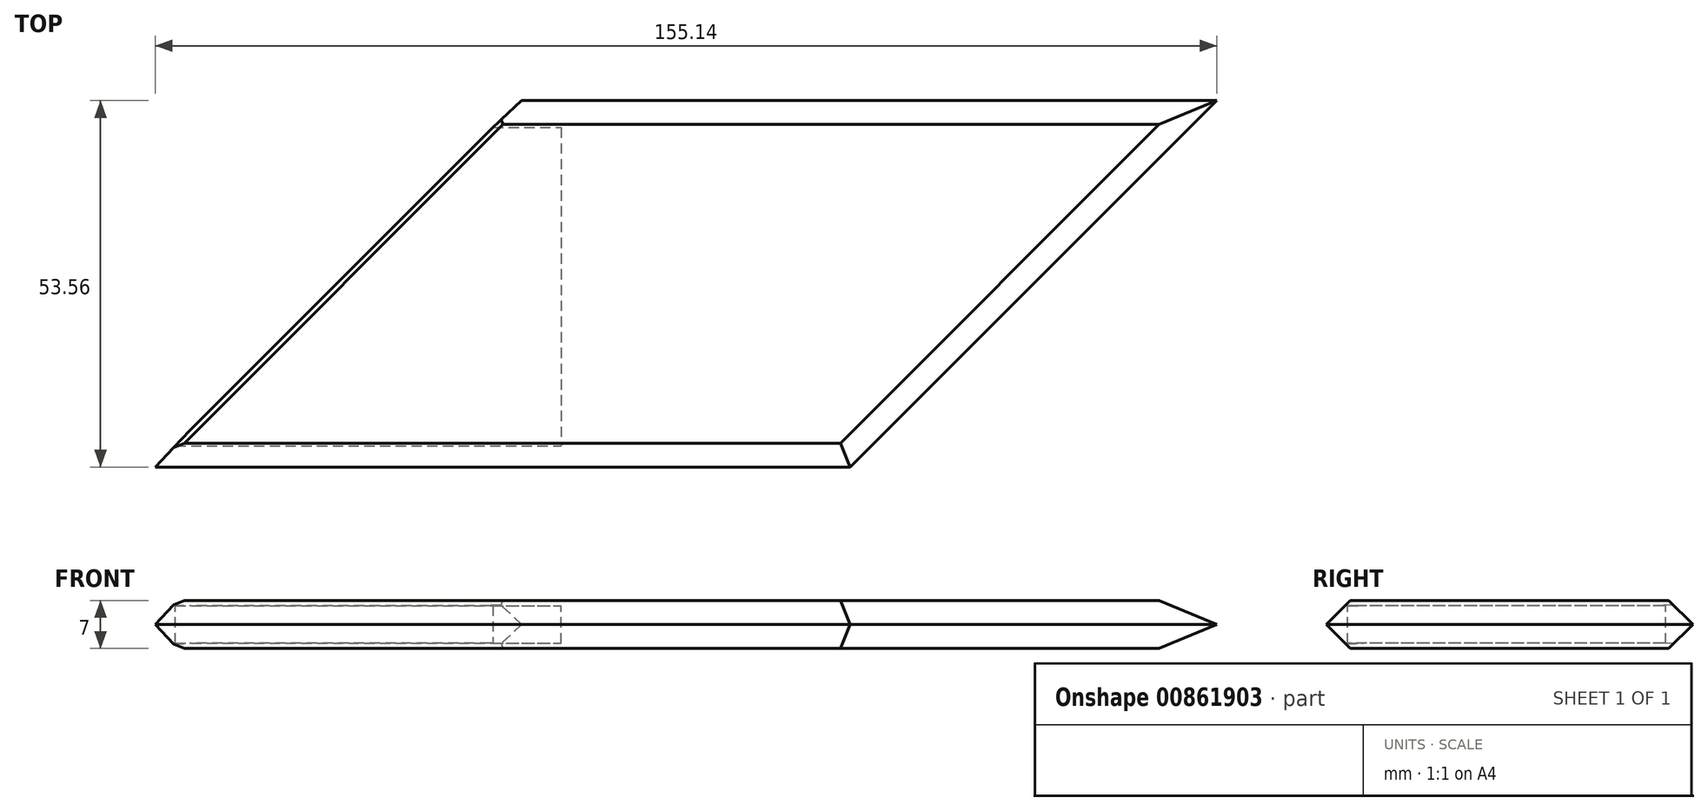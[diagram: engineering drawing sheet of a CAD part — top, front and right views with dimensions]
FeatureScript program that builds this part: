
annotation { "Feature Type Name" : "Feature", "Feature Type Description" : "" }
export const myFeature = defineFeature(function(context is Context, id is Id, definition is map)
    precondition{}
    {
        {
            var Q0;
            Q0=qCreatedBy(makeId("Top.planeOp"),FACE);
            cPlane(context, id + "F0", {"entities" : qUnion([Q0]), "cplaneType" : CPlaneType.OFFSET, "offset" : 3.5 * mm, "width" : 150 * mm, "height" : 150 * mm});
        }
        {
            var Q0;
            Q0=qCreatedBy(id+"F0.planeOp",FACE);
            var sketch = newSketch(context, id + "F1", { "sketchPlane" : qUnion([Q0])});
            skLineSegment(sketch, "E0", {"start": v(32.38, -28.28) * mm, "end": v(88.95, 28.28) * mm});
            skLineSegment(sketch, "E1", {"start": v(32.38, -28.28) * mm, "end": v(-77.62, -28.28) * mm});
            skLineSegment(sketch, "E2", {"start": v(88.95, 28.28) * mm, "end": v(-21.05, 28.28) * mm});
            skLineSegment(sketch, "E3", {"start": v(-21.05, 28.28) * mm, "end": v(-77.62, -28.28) * mm});
            skLineSegment(sketch, "E4", {"start": v(32.38, -28.28) * mm, "end": v(60.67, 0) * mm});
            skLineSegment(sketch, "E5", {"start": v(-9.09, -28.28) * mm, "end": v(-9.09, 28.28) * mm, "construction": true});
            skLineSegment(sketch, "E6", {"start": v(11.8, -28.28) * mm, "end": v(11.8, 0) * mm});
            skSolve(sketch);
        }
        {
            var Q0;
            Q0=makeQuery(id+"F1.imprint","IMPRINT",FACE,{"disambiguationData":[TD([[makeQuery(id+"F1.imprint","IMPRINT",EDGE,{"derivedFrom":sQuery(id+"F1.wireOp",EDGE,"E0")}),1.0]])]});
            extrude(context, id + "F2", {"entities" : qUnion([Q0]), "depth" : 3.5 * mm, "offsetDistance" : 25 * mm});
        }
        {
            var Q0;
            Q0=makeQuery(id+"F2.opExtrude","CAP_FACE",FACE,{"disambiguationData":[OSD([sQuery(id+"F1.wireOp",EDGE,"E0"),sQuery(id+"F1.wireOp",EDGE,"E1"),sQuery(id+"F1.wireOp",EDGE,"E2"),sQuery(id+"F1.wireOp",EDGE,"E3")])],"isStart":true});
            chamfer(context, id + "F3", {"entities" : qUnion([Q0]), "width" : 5 * mm, "tangentPropagation" : true});
        }
        {
            var Q0;
            Q0=makeQuery(id+"F2.opExtrude","CAP_FACE",FACE,{"disambiguationData":[OSD([sQuery(id+"F1.wireOp",EDGE,"E0"),sQuery(id+"F1.wireOp",EDGE,"E1"),sQuery(id+"F1.wireOp",EDGE,"E2"),sQuery(id+"F1.wireOp",EDGE,"E3")])],"isStart":true});
            var sketch = newSketch(context, id + "F4", { "sketchPlane" : qUnion([Q0])});
            skLineSegment(sketch, "E7", {"start": v(-60.92, 17.37) * mm, "end": v(-71.56, 28.64) * mm});
            skLineSegment(sketch, "E8", {"start": v(-71.56, 28.64) * mm, "end": v(-75.4, 28.64) * mm});
            skLineSegment(sketch, "E9", {"start": v(-75.4, 28.64) * mm, "end": v(-72.63, 14.89) * mm});
            skLineSegment(sketch, "E10", {"start": v(-72.63, 14.89) * mm, "end": v(-60.92, 17.37) * mm});
            skLineSegment(sketch, "E11.MirrorCS", {"start": v(-71.56, -28.64) * mm, "end": v(-75.4, -28.64) * mm});
            skLineSegment(sketch, "E12.MirrorCS", {"start": v(-75.4, -28.64) * mm, "end": v(-72.63, -14.89) * mm});
            skLineSegment(sketch, "E13.MirrorCS", {"start": v(-72.63, -14.89) * mm, "end": v(-60.92, -17.37) * mm});
            skLineSegment(sketch, "E14.MirrorCS", {"start": v(-60.92, -17.37) * mm, "end": v(-71.56, -28.64) * mm});
            skLineSegment(sketch, "E15", {"start": v(-42.26, 0) * mm, "end": v(-56.59, -14.32) * mm});
            skLineSegment(sketch, "E16", {"start": v(-42.26, 0) * mm, "end": v(-58.96, 0) * mm});
            skLineSegment(sketch, "E17.MirrorCS", {"start": v(-27.38, -30.37) * mm, "end": v(-24.9, -18.65) * mm});
            skLineSegment(sketch, "E18.MirrorCS", {"start": v(-13.62, -33.13) * mm, "end": v(-27.38, -30.37) * mm});
            skLineSegment(sketch, "E19.MirrorCS", {"start": v(-24.9, -18.65) * mm, "end": v(-13.62, -29.3) * mm});
            skLineSegment(sketch, "E20.MirrorCS", {"start": v(-13.62, -29.3) * mm, "end": v(-13.62, -33.13) * mm});
            skSolve(sketch);
        }
        {
            var Q0;
            Q0=makeQuery(id+"F2.opExtrude","CAP_FACE",FACE,{"disambiguationData":[OSD([sQuery(id+"F1.wireOp",EDGE,"E0"),sQuery(id+"F1.wireOp",EDGE,"E1"),sQuery(id+"F1.wireOp",EDGE,"E2"),sQuery(id+"F1.wireOp",EDGE,"E3"),sQuery(id+"F1.wireOp",EDGE,"E4")])],"isStart":false});
            var sketch = newSketch(context, id + "F5", { "sketchPlane" : qUnion([Q0])});
            skLineSegment(sketch, "E21.bottom", {"start": v(-67.31, 22.83) * mm, "end": v(27.88, 22.83) * mm});
            skLineSegment(sketch, "E21.top", {"start": v(-67.31, -23.67) * mm, "end": v(27.88, -23.67) * mm});
            skLineSegment(sketch, "E21.left", {"start": v(-67.31, 22.83) * mm, "end": v(-67.31, -23.67) * mm});
            skLineSegment(sketch, "E21.right", {"start": v(27.88, 22.83) * mm, "end": v(27.88, -23.67) * mm});
            skSolve(sketch);
        }
        {
            var Q0;
            Q0 = qSketchRegion(id + "F5", true);
            extrude(context, id + "F6", {"entities" : qUnion([Q0]), "operationType" : NewBodyOperationType.REMOVE, "oppositeDirection" : true, "depth" : 2.75 * mm, "offsetDistance" : 25 * mm});
        }
        {
            var Q0;
            Q0=makeQuery(id+"F4.imprint","IMPRINT",FACE,{"disambiguationData":[TD([[makeQuery(id+"F4.imprint","IMPRINT",EDGE,{"derivedFrom":sQuery(id+"F4.wireOp",EDGE,"E17.MirrorCS")}),-1.0]])]});
            var Q1;
            Q1=makeQuery(id+"F4.imprint","IMPRINT",FACE,{"disambiguationData":[TD([[makeQuery(id+"F4.imprint","IMPRINT",EDGE,{"derivedFrom":sQuery(id+"F4.wireOp",EDGE,"E7")}),1.0]])]});
            extrude(context, id + "F7", {"entities" : qUnion([Q0, Q1]), "operationType" : NewBodyOperationType.REMOVE, "oppositeDirection" : true, "depth" : 25 * mm, "offsetDistance" : 25 * mm});
        }
        {
            var Q0;
            Q0=makeQuery(id+"F2.opExtrude","SWEPT_BODY",BODY,{"disambiguationData":[OSD([sQuery(id+"F1.wireOp",EDGE,"E0"),sQuery(id+"F1.wireOp",EDGE,"E1"),sQuery(id+"F1.wireOp",EDGE,"E2"),sQuery(id+"F1.wireOp",EDGE,"E3"),sQuery(id+"F1.wireOp",EDGE,"E4")])]});
            var Q1;
            {var subQ2=sQuery(id+"F5.wireOp",EDGE,"E21.top");Q1=makeQuery(id+"F5.imprint","IMPRINT",FACE,{"disambiguationData":[TD([[makeQuery(id+"F5.imprint","IMPRINT",EDGE,{"derivedFrom":subQ2}),-1.0]])]});}
            mirror(context, id + "F8", {"entities" : qUnion([Q0]), "mirrorPlane" : qUnion([Q1])});
        }
        {
            var Q0;
            Q0=makeQuery(id+"F6.boolean.opBoolean","COPY",FACE,{"derivedFrom":makeQuery(id+"F6.opExtrude","SWEPT_FACE",FACE,{"disambiguationData":[OSD([sQuery(id+"F5.wireOp",EDGE,"E21.right")])]})});
            extrude(context, id + "F9", {"entities" : qUnion([Q0]), "operationType" : NewBodyOperationType.ADD, "depth" : 38.4 * mm, "offsetDistance" : 25 * mm});
        }
        {
            var Q0;
            Q0=makeQuery(id+"F8.opPattern","COPY",FACE,{"derivedFrom":makeQuery(id+"F6.boolean.opBoolean","COPY",FACE,{"derivedFrom":makeQuery(id+"F6.opExtrude","SWEPT_FACE",FACE,{"disambiguationData":[OSD([sQuery(id+"F5.wireOp",EDGE,"E21.right")])]})}),"instanceName":"1"});
            extrude(context, id + "F10", {"entities" : qUnion([Q0]), "operationType" : NewBodyOperationType.ADD, "depth" : 38.4 * mm, "offsetDistance" : 25 * mm});
        }
    });
